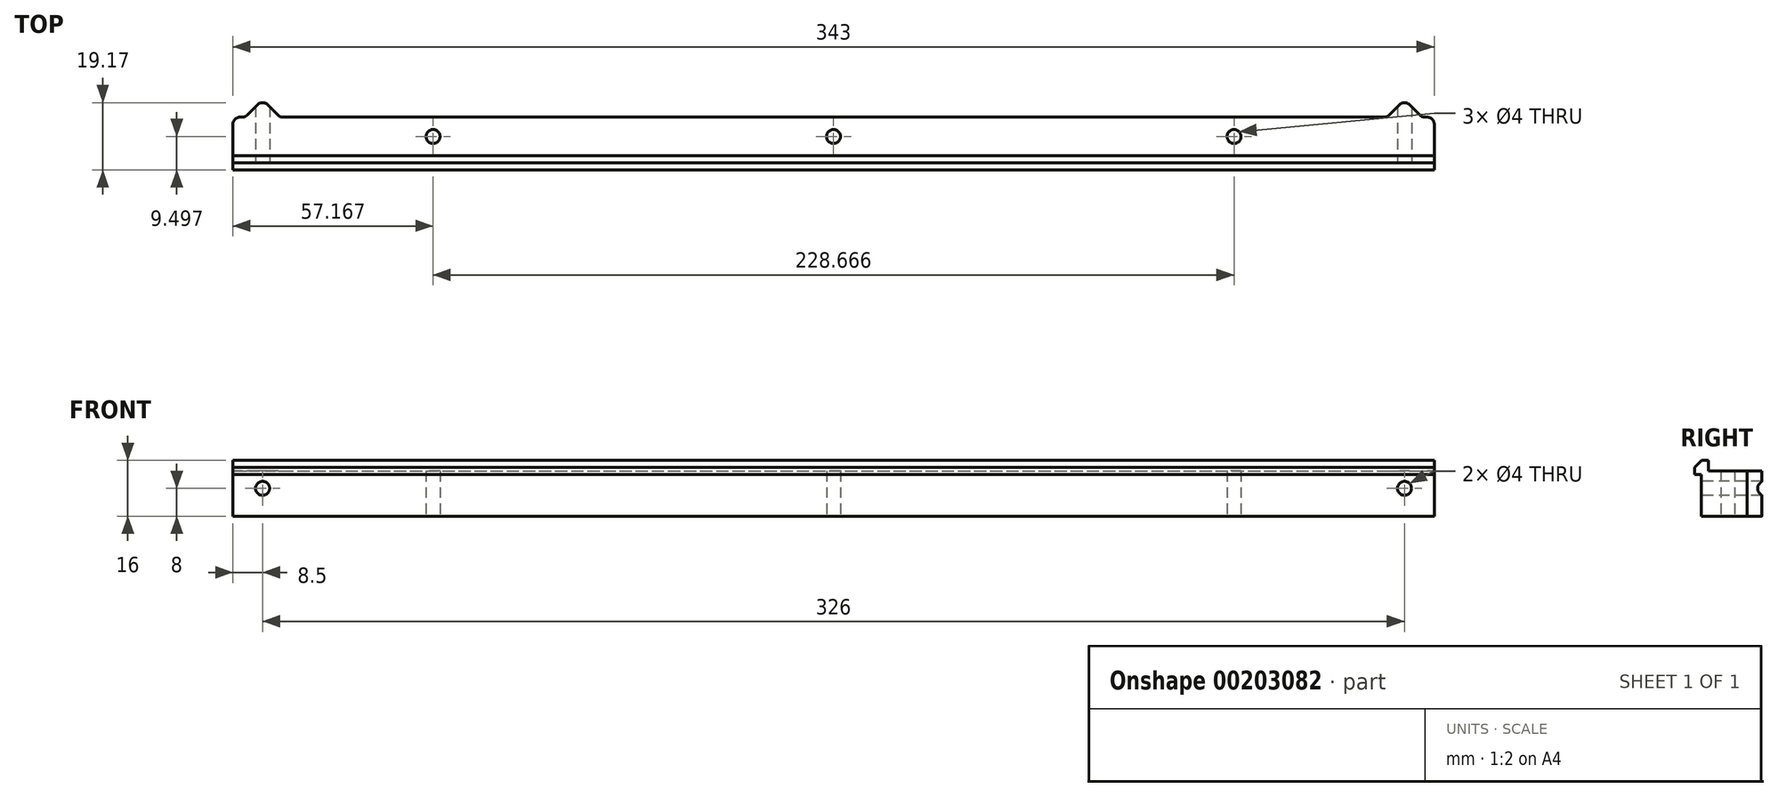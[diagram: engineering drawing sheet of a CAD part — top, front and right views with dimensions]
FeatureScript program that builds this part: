
annotation { "Feature Type Name" : "Feature", "Feature Type Description" : "" }
export const myFeature = defineFeature(function(context is Context, id is Id, definition is map)
    precondition{}
    {
        {
            var Q0;
            Q0=qCreatedBy(makeId("Top.planeOp"),FACE);
            var sketch = newSketch(context, id + "F0", { "sketchPlane" : qUnion([Q0])});
            skLineSegment(sketch, "E0.top", {"start": v(-171.5, -131.22) * mm, "end": v(171.5, -131.22) * mm});
            skPoint(sketch, "E1.visualSharp", {"position": v(-186.5, -131.22) * mm});
            skLineSegment(sketch, "E2.top", {"start": v(-154.5, -116.22) * mm, "end": v(157.17, -116.22) * mm});
            skLineSegment(sketch, "E3", {"start": v(-154.5, -116.22) * mm, "end": v(-157.17, -116.22) * mm});
            skLineSegment(sketch, "E4", {"start": v(-158.59, -115.64) * mm, "end": v(-161.59, -112.64) * mm});
            skLineSegment(sketch, "E5", {"start": v(-164.41, -112.64) * mm, "end": v(-167.41, -115.64) * mm});
            skLineSegment(sketch, "E6", {"start": v(-168.83, -116.22) * mm, "end": v(-169.5, -116.22) * mm});
            skLineSegment(sketch, "E7", {"start": v(-171.5, -118.22) * mm, "end": v(-171.5, -127.73) * mm});
            skArc(sketch, "E8.filletArc", {"start": v(-161.59, -112.64) * mm, "mid": v(-163, -112.05) * mm, "end": v(-164.41, -112.64) * mm});
            skPoint(sketch, "E9.visualSharp", {"position": v(-158, -116.22) * mm});
            skArc(sketch, "E9.filletArc", {"start": v(-158.59, -115.64) * mm, "mid": v(-157.94, -116.07) * mm, "end": v(-157.17, -116.22) * mm});
            skPoint(sketch, "E10.visualSharp", {"position": v(-168, -116.22) * mm});
            skArc(sketch, "E10.filletArc", {"start": v(-168.83, -116.22) * mm, "mid": v(-168.06, -116.07) * mm, "end": v(-167.41, -115.64) * mm});
            skPoint(sketch, "E11.visualSharp", {"position": v(-171.5, -116.22) * mm});
            skArc(sketch, "E11.filletArc", {"start": v(-169.5, -116.22) * mm, "mid": v(-170.91, -116.8) * mm, "end": v(-171.5, -118.22) * mm});
            skLineSegment(sketch, "E12", {"start": v(-171.5, -127.73) * mm, "end": v(-171.5, -131.22) * mm});
            skArc(sketch, "E13.MirrorCS", {"start": v(158.59, -115.64) * mm, "mid": v(157.94, -116.07) * mm, "end": v(157.17, -116.22) * mm});
            skLineSegment(sketch, "E14.MirrorCS", {"start": v(158.59, -115.64) * mm, "end": v(161.59, -112.64) * mm});
            skArc(sketch, "E15.MirrorCS", {"start": v(161.59, -112.64) * mm, "mid": v(163, -112.05) * mm, "end": v(164.41, -112.64) * mm});
            skLineSegment(sketch, "E16.MirrorCS", {"start": v(164.41, -112.64) * mm, "end": v(167.41, -115.64) * mm});
            skArc(sketch, "E17.MirrorCS", {"start": v(168.83, -116.22) * mm, "mid": v(168.06, -116.07) * mm, "end": v(167.41, -115.64) * mm});
            skArc(sketch, "E18.MirrorCS", {"start": v(169.5, -116.22) * mm, "mid": v(170.91, -116.8) * mm, "end": v(171.5, -118.22) * mm});
            skLineSegment(sketch, "E19.MirrorCS", {"start": v(171.5, -118.22) * mm, "end": v(171.5, -127.73) * mm});
            skLineSegment(sketch, "E20.MirrorCS", {"start": v(171.5, -127.73) * mm, "end": v(171.5, -131.22) * mm});
            skLineSegment(sketch, "E21.trimOffspring", {"start": v(168.83, -116.22) * mm, "end": v(169.5, -116.22) * mm});
            skPoint(sketch, "E22.MirrorCS.end.orphan", {"position": v(157.17, -116.22) * mm});
            skPoint(sketch, "E22.MirrorCS.start.orphan", {"position": v(154.5, -116.22) * mm});
            skPoint(sketch, "E23.MirrorCS.end.orphan", {"position": v(169.5, -116.22) * mm});
            skCircle(sketch, "E24", {"center": v(-114.33, -121.72) * mm, "radius": 2 * mm});
            skCircle(sketch, "E25", {"center": v(0, -121.72) * mm, "radius": 2 * mm});
            skPoint(sketch, "E25.centerSnap0", {"position": v(0, -131.22) * mm});
            skCircle(sketch, "E26", {"center": v(114.33, -121.72) * mm, "radius": 2 * mm});
            skSolve(sketch);
        }
        {
            var Q0;
            Q0 = qSketchRegion(id + "F0", true);
            extrude(context, id + "F1", {"entities" : qUnion([Q0]), "depth" : 16 * mm});
        }
        {
            var Q0;
            Q0=makeQuery(id+"F1.opExtrude","CAP_EDGE",EDGE,{"disambiguationData":[OSD([sQuery(id+"F0.wireOp",EDGE,"E0.top")])],"isStart":false});
            chamfer(context, id + "F2", {"entities" : qUnion([Q0]), "width" : 2 * mm, "tangentPropagation" : true});
        }
        {
            var Q0;
            Q0=makeQuery(id+"F1.opExtrude","CAP_FACE",FACE,{"disambiguationData":[OSD([sQuery(id+"F0.wireOp",EDGE,"E0.bottom"),sQuery(id+"F0.wireOp",EDGE,"E0.top"),sQuery(id+"F0.wireOp",EDGE,"E0.left"),sQuery(id+"F0.wireOp",EDGE,"E0.right"),sQuery(id+"F0.wireOp",EDGE,"E1.filletArc"),sQuery(id+"F0.wireOp",EDGE,"b9720682-2eae-4cc5-adf0-be07a7641b49.filletArc"),sQuery(id+"F0.wireOp",EDGE,"0606984b-c95c-4b6f-a22b-b9101ec73185.filletArc"),sQuery(id+"F0.wireOp",EDGE,"ed30f497-0052-4637-aeee-16b670f2d78a.filletArc"),sQuery(id+"F0.wireOp",EDGE,"E2.bottom"),sQuery(id+"F0.wireOp",EDGE,"E2.top"),sQuery(id+"F0.wireOp",EDGE,"E2.left"),sQuery(id+"F0.wireOp",EDGE,"E2.right")])],"isStart":false});
            var sketch = newSketch(context, id + "F3", { "sketchPlane" : qUnion([Q0])});
            skLineSegment(sketch, "E27.3", {"start": v(-174.5, -127.22) * mm, "end": v(174.5, -127.22) * mm});
            skLineSegment(sketch, "E28", {"start": v(-174.5, -127.22) * mm, "end": v(-174.5, -111.22) * mm});
            skLineSegment(sketch, "E29", {"start": v(174.5, -127.22) * mm, "end": v(174.5, -111.22) * mm});
            skLineSegment(sketch, "E30", {"start": v(-174.5, -111.22) * mm, "end": v(174.5, -111.22) * mm});
            skSolve(sketch);
        }
        {
            var Q0;
            Q0=qSketchRegion(id+"F3",true);
            extrude(context, id + "F4", {"entities" : qUnion([Q0]), "operationType" : NewBodyOperationType.REMOVE, "oppositeDirection" : true, "depth" : 3.1 * mm});
        }
        {
            var Q0;
            Q0=makeQuery(id+"F0.imprint","IMPRINT",FACE,{"disambiguationData":[TD([[makeQuery(id+"F0.imprint","IMPRINT",EDGE,{"derivedFrom":sQuery(id+"F0.wireOp",EDGE,"E0.top")}),1.0]])]});
            var sketch = newSketch(context, id + "F5", { "sketchPlane" : qUnion([Q0])});
            skLineSegment(sketch, "E31.5", {"start": v(-172.6, -129.32) * mm, "end": v(172.6, -129.32) * mm});
            skLineSegment(sketch, "E32.5", {"start": v(-172.6, -134.32) * mm, "end": v(172.6, -134.32) * mm});
            skLineSegment(sketch, "E33", {"start": v(-172.6, -129.32) * mm, "end": v(-172.6, -134.32) * mm});
            skLineSegment(sketch, "E34", {"start": v(172.6, -129.32) * mm, "end": v(172.6, -134.32) * mm});
            skSolve(sketch);
        }
        {
            var Q0;
            Q0=qSketchRegion(id+"F5",true);
            extrude(context, id + "F6", {"entities" : qUnion([Q0]), "operationType" : NewBodyOperationType.REMOVE, "depth" : 12 * mm});
        }
        {
            var Q0;
            Q0=makeQuery(id+"F6.boolean.opBoolean","COPY",FACE,{"derivedFrom":makeQuery(id+"F6.opExtrude","SWEPT_FACE",FACE,{"disambiguationData":[OSD([sQuery(id+"F5.wireOp",EDGE,"E31.5")])]})});
            var sketch = newSketch(context, id + "F7", { "sketchPlane" : qUnion([Q0])});
            skCircle(sketch, "E35", {"center": v(-163, 8) * mm, "radius": 2 * mm});
            skCircle(sketch, "E36.MirrorC", {"center": v(163, 8) * mm, "radius": 2 * mm});
            skSolve(sketch);
        }
        {
            var Q0;
            Q0=qSketchRegion(id+"F7",true);
            extrude(context, id + "F8", {"entities" : qUnion([Q0]), "operationType" : NewBodyOperationType.REMOVE, "endBound" : BoundingType.THROUGH_ALL, "oppositeDirection" : true, "depth" : 25 * mm});
        }
    });
